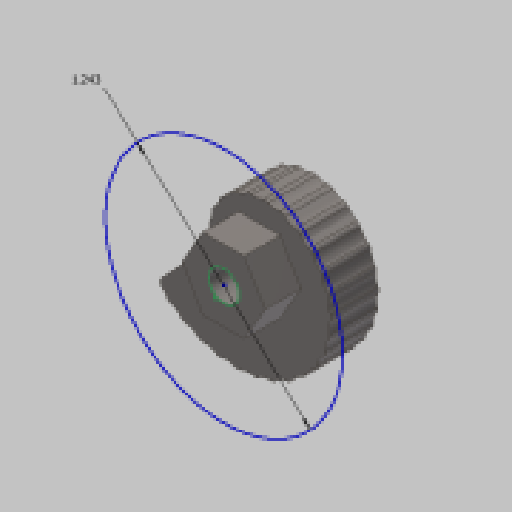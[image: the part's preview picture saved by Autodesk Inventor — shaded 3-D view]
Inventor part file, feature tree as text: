
AUTODESK INVENTOR PART (.ipt)
format: ipt  version: 2023.5 (Build 275446000, 446)  size: 209,920 bytes
history: native  units: in
note: dims shown in document units (in); Inventor stores cm internally (conversion verified against a paired STEP export)
features: fillet x1
ambient origin geometry x8: Origin, YZ Plane, XZ Plane, XY Plane, X Axis, Y Axis, Z Axis, Center Point
bodies: Solid1 (feature_tree)
feature tree (1):
  fillet  "Fillet1"  [1 undecoded]
note: 1 required parameter value undecoded (feature->parameter linkage not recoverable at this tier; creation-order binding heuristic only, values carry confidence <= 0.55)
